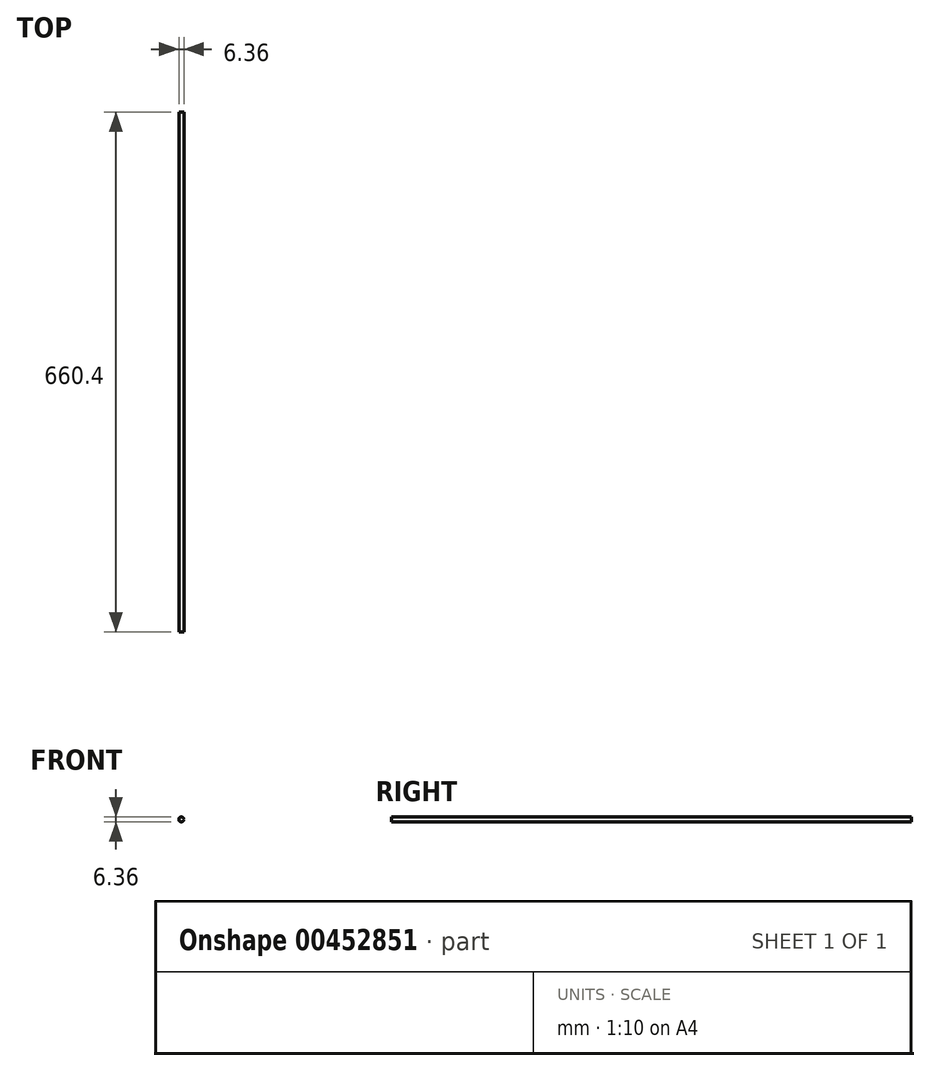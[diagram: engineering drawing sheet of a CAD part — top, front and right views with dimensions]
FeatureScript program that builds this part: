
annotation { "Feature Type Name" : "Feature", "Feature Type Description" : "" }
export const myFeature = defineFeature(function(context is Context, id is Id, definition is map)
    precondition{}
    {
        {
            var Q0;
            Q0=qCreatedBy(makeId("Front.planeOp"),FACE);
            var sketch = newSketch(context, id + "F0", { "sketchPlane" : qUnion([Q0])});
            skCircle(sketch, "E0", {"center": v(0, 0) * mm, "radius": 3.18 * mm});
            skSolve(sketch);
        }
        {
            var Q0;
            Q0 = qSketchRegion(id + "F0", true);
            extrude(context, id + "F1", {"entities" : qUnion([Q0]), "endBound" : BoundingType.SYMMETRIC, "depth" : 660.4 * mm});
        }
    });
